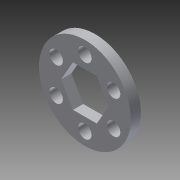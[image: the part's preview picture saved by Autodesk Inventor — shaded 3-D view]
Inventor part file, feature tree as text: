
AUTODESK INVENTOR PART (.ipt)
format: ipt  version: 2014 (Build 180170000, 170)  size: 102,912 bytes
history: native  units: in
note: dims shown in document units (in); Inventor stores cm internally (conversion verified against a paired STEP export)
features: extrude x1, sketch x1
ambient origin geometry x8: Origin, YZ Plane, XZ Plane, XY Plane, X Axis, Y Axis, Z Axis, Center Point
bodies: Solid1 (feature_tree)
feature tree (2):
  extrude  "Extrusion1"  Depth=0.504in
  sketch  "Sketch1"  dims[d0=1.125in d1=0.504in d2=0.164in d3=0.4062in d4=2.3622in d6=360.0deg d8=0.125in d9=0.0in]
